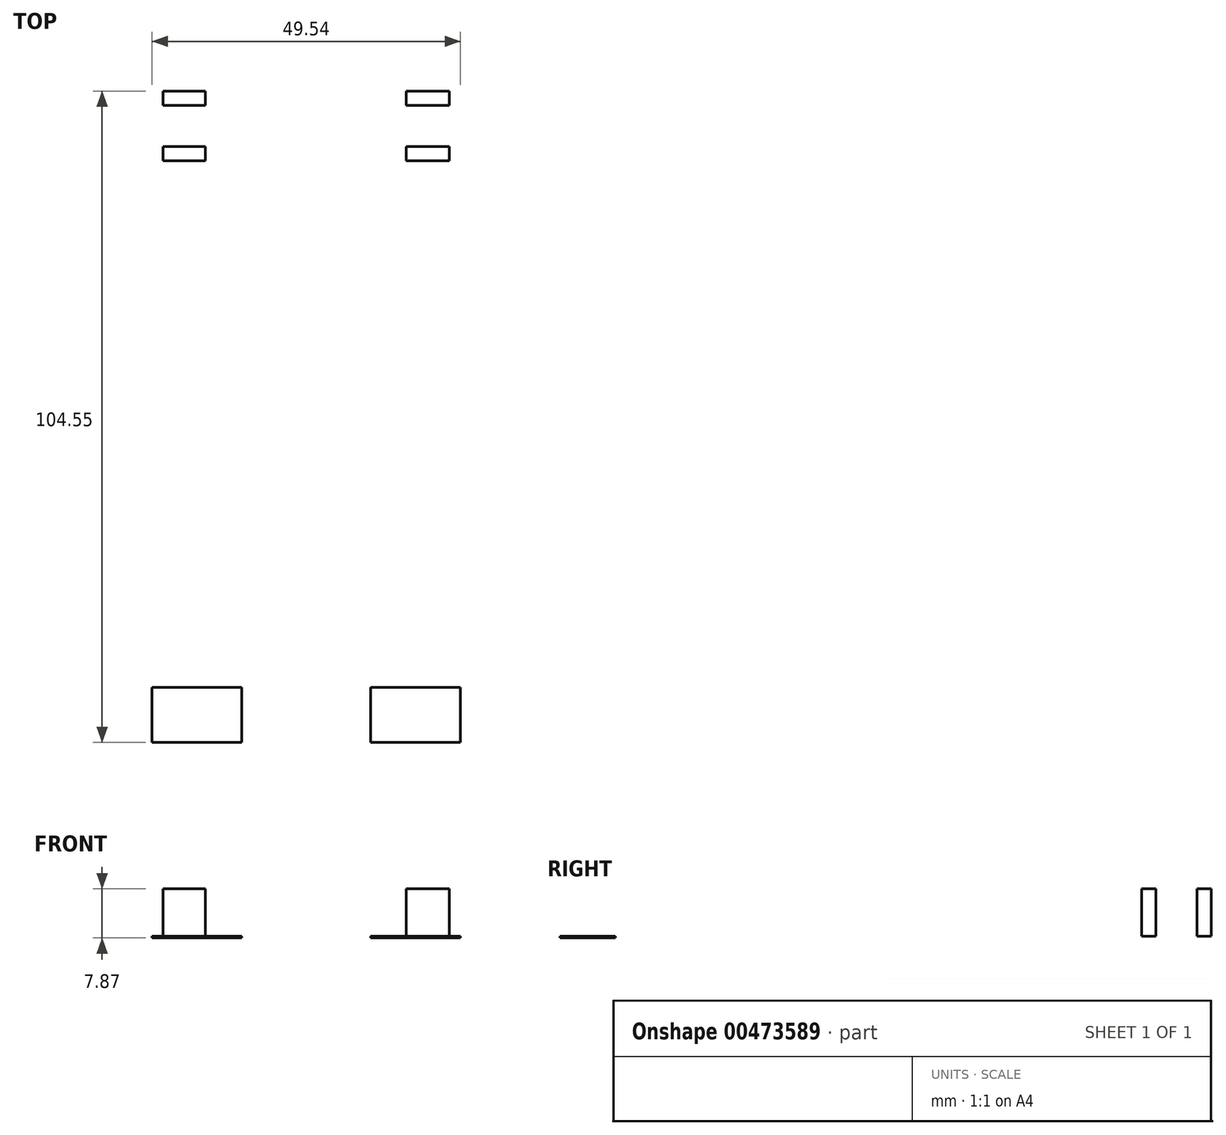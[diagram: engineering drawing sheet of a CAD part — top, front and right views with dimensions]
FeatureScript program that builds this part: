
annotation { "Feature Type Name" : "Feature", "Feature Type Description" : "" }
export const myFeature = defineFeature(function(context is Context, id is Id, definition is map)
    precondition{}
    {
        {
            var Q0;
            Q0=qCreatedBy(makeId("Top.planeOp"),FACE);
            var sketch = newSketch(context, id + "F0", { "sketchPlane" : qUnion([Q0])});
            skLineSegment(sketch, "E0.bottom", {"start": v(24.77, -56.2) * mm, "end": v(-24.77, -56.2) * mm});
            skLineSegment(sketch, "E0.top", {"start": v(24.77, 56.2) * mm, "end": v(-24.77, 56.2) * mm});
            skLineSegment(sketch, "E0.left", {"start": v(24.77, -56.2) * mm, "end": v(24.77, 56.2) * mm});
            skLineSegment(sketch, "E0.right", {"start": v(-24.77, -56.2) * mm, "end": v(-24.77, 56.2) * mm});
            skPoint(sketch, "E0.middle", {"position": v(0, 0) * mm});
            skLineSegment(sketch, "E1.bottom", {"start": v(-24.77, 49.36) * mm, "end": v(-10.35, 49.36) * mm});
            skLineSegment(sketch, "E1.top", {"start": v(-24.77, 56.2) * mm, "end": v(-10.35, 56.2) * mm});
            skLineSegment(sketch, "E1.left", {"start": v(-24.77, 49.36) * mm, "end": v(-24.77, 56.2) * mm});
            skLineSegment(sketch, "E1.right", {"start": v(-10.35, 49.36) * mm, "end": v(-10.35, 56.2) * mm});
            skLineSegment(sketch, "E2.bottom", {"start": v(24.77, 49.36) * mm, "end": v(10.35, 49.36) * mm});
            skLineSegment(sketch, "E2.top", {"start": v(24.77, 56.2) * mm, "end": v(10.35, 56.2) * mm});
            skLineSegment(sketch, "E2.left", {"start": v(24.77, 49.36) * mm, "end": v(24.77, 56.2) * mm});
            skLineSegment(sketch, "E2.right", {"start": v(10.35, 49.36) * mm, "end": v(10.35, 56.2) * mm});
            skLineSegment(sketch, "E3.bottom", {"start": v(10.35, -56.2) * mm, "end": v(24.77, -56.2) * mm});
            skLineSegment(sketch, "E3.top", {"start": v(10.35, -47.32) * mm, "end": v(24.77, -47.32) * mm});
            skLineSegment(sketch, "E3.left", {"start": v(10.35, -56.2) * mm, "end": v(10.35, -47.32) * mm});
            skLineSegment(sketch, "E3.right", {"start": v(24.77, -56.2) * mm, "end": v(24.77, -47.32) * mm});
            skLineSegment(sketch, "E4.bottom", {"start": v(-10.35, -47.32) * mm, "end": v(-24.77, -47.32) * mm});
            skLineSegment(sketch, "E4.top", {"start": v(-10.35, -56.2) * mm, "end": v(-24.77, -56.2) * mm});
            skLineSegment(sketch, "E4.left", {"start": v(-10.35, -47.32) * mm, "end": v(-10.35, -56.2) * mm});
            skLineSegment(sketch, "E4.right", {"start": v(-24.77, -47.32) * mm, "end": v(-24.77, -56.2) * mm});
            skLineSegment(sketch, "E5.bottom", {"start": v(-24.77, 34.94) * mm, "end": v(-14.61, 34.94) * mm});
            skLineSegment(sketch, "E5.top", {"start": v(-24.77, -33.64) * mm, "end": v(-14.61, -33.64) * mm});
            skLineSegment(sketch, "E5.left", {"start": v(-24.77, 34.94) * mm, "end": v(-24.77, -33.64) * mm});
            skLineSegment(sketch, "E5.right", {"start": v(-14.61, 34.94) * mm, "end": v(-14.61, -33.64) * mm});
            skLineSegment(sketch, "E6.bottom", {"start": v(24.77, 34.94) * mm, "end": v(14.61, 34.94) * mm});
            skLineSegment(sketch, "E6.top", {"start": v(24.77, -33.64) * mm, "end": v(14.61, -33.64) * mm});
            skLineSegment(sketch, "E6.left", {"start": v(24.77, 34.94) * mm, "end": v(24.77, -33.64) * mm});
            skLineSegment(sketch, "E6.right", {"start": v(14.61, 34.94) * mm, "end": v(14.61, -33.64) * mm});
            skSolve(sketch);
        }
        {
            var Q0;
            Q0=makeQuery(id+"F0.imprint","IMPRINT",FACE,{"disambiguationData":[TD([[makeQuery(id+"F0.imprint","IMPRINT",EDGE,{"derivedFrom":sQuery(id+"F0.wireOp",EDGE,"E0.bottom")}),-1.0]])]});
            extrude(context, id + "F1", {"entities" : qUnion([Q0]), "oppositeDirection" : true, "depth" : 0.25 * mm});
        }
        {
            var Q0;
            Q0=makeQuery(id+"F1.opExtrude","CAP_FACE",FACE,{"disambiguationData":[OSD([sQuery(id+"F0.wireOp",EDGE,"E0.bottom"),sQuery(id+"F0.wireOp",EDGE,"E0.top"),sQuery(id+"F0.wireOp",EDGE,"E0.left"),sQuery(id+"F0.wireOp",EDGE,"E0.right"),sQuery(id+"F0.wireOp",EDGE,"E1.bottom"),sQuery(id+"F0.wireOp",EDGE,"E1.right"),sQuery(id+"F0.wireOp",EDGE,"E2.bottom"),sQuery(id+"F0.wireOp",EDGE,"E2.right"),sQuery(id+"F0.wireOp",EDGE,"E3.top"),sQuery(id+"F0.wireOp",EDGE,"E3.left"),sQuery(id+"F0.wireOp",EDGE,"E4.bottom"),sQuery(id+"F0.wireOp",EDGE,"E4.left"),sQuery(id+"F0.wireOp",EDGE,"E5.bottom"),sQuery(id+"F0.wireOp",EDGE,"E5.top"),sQuery(id+"F0.wireOp",EDGE,"E5.right"),sQuery(id+"F0.wireOp",EDGE,"E6.bottom"),sQuery(id+"F0.wireOp",EDGE,"E6.top"),sQuery(id+"F0.wireOp",EDGE,"E6.right")])],"isStart":true});
            var sketch = newSketch(context, id + "F2", { "sketchPlane" : qUnion([Q0])});
            skLineSegment(sketch, "E7.bottom", {"start": v(-23, 48.36) * mm, "end": v(-16.2, 48.36) * mm});
            skLineSegment(sketch, "E7.top", {"start": v(-23, 46.07) * mm, "end": v(-16.2, 46.07) * mm});
            skLineSegment(sketch, "E7.left", {"start": v(-23, 48.36) * mm, "end": v(-23, 46.07) * mm});
            skLineSegment(sketch, "E7.right", {"start": v(-16.2, 48.36) * mm, "end": v(-16.2, 46.07) * mm});
            skLineSegment(sketch, "E8.bottom", {"start": v(-23, 39.47) * mm, "end": v(-16.2, 39.47) * mm});
            skLineSegment(sketch, "E8.top", {"start": v(-23, 37.18) * mm, "end": v(-16.2, 37.18) * mm});
            skLineSegment(sketch, "E8.left", {"start": v(-23, 39.47) * mm, "end": v(-23, 37.18) * mm});
            skLineSegment(sketch, "E8.right", {"start": v(-16.2, 39.47) * mm, "end": v(-16.2, 37.18) * mm});
            skLineSegment(sketch, "E9.bottom", {"start": v(16.06, 48.36) * mm, "end": v(23, 48.36) * mm});
            skLineSegment(sketch, "E9.top", {"start": v(16.06, 46.07) * mm, "end": v(23, 46.07) * mm});
            skLineSegment(sketch, "E9.left", {"start": v(16.06, 48.36) * mm, "end": v(16.06, 46.07) * mm});
            skLineSegment(sketch, "E9.right", {"start": v(23, 48.36) * mm, "end": v(23, 46.07) * mm});
            skLineSegment(sketch, "E10.bottom", {"start": v(16.06, 39.47) * mm, "end": v(23, 39.47) * mm});
            skLineSegment(sketch, "E10.top", {"start": v(16.06, 37.18) * mm, "end": v(23, 37.18) * mm});
            skLineSegment(sketch, "E10.left", {"start": v(16.06, 39.47) * mm, "end": v(16.06, 37.18) * mm});
            skLineSegment(sketch, "E10.right", {"start": v(23, 39.47) * mm, "end": v(23, 37.18) * mm});
            skSolve(sketch);
        }
        {
            var Q0;
            Q0=makeQuery(id+"F2.imprint","IMPRINT",FACE,{"disambiguationData":[TD([[makeQuery(id+"F2.imprint","IMPRINT",EDGE,{"derivedFrom":sQuery(id+"F2.wireOp",EDGE,"E7.bottom")}),-1.0]])]});
            var Q1;
            Q1=makeQuery(id+"F2.imprint","IMPRINT",FACE,{"disambiguationData":[TD([[makeQuery(id+"F2.imprint","IMPRINT",EDGE,{"derivedFrom":sQuery(id+"F2.wireOp",EDGE,"E8.bottom")}),-1.0]])]});
            var Q2;
            Q2=makeQuery(id+"F2.imprint","IMPRINT",FACE,{"disambiguationData":[TD([[makeQuery(id+"F2.imprint","IMPRINT",EDGE,{"derivedFrom":sQuery(id+"F2.wireOp",EDGE,"E10.bottom")}),-1.0]])]});
            var Q3;
            Q3=makeQuery(id+"F2.imprint","IMPRINT",FACE,{"disambiguationData":[TD([[makeQuery(id+"F2.imprint","IMPRINT",EDGE,{"derivedFrom":sQuery(id+"F2.wireOp",EDGE,"E9.bottom")}),-1.0]])]});
            extrude(context, id + "F3", {"entities" : qUnion([Q0, Q1, Q2, Q3]), "operationType" : NewBodyOperationType.ADD, "depth" : 7.62 * mm});
        }
    });
